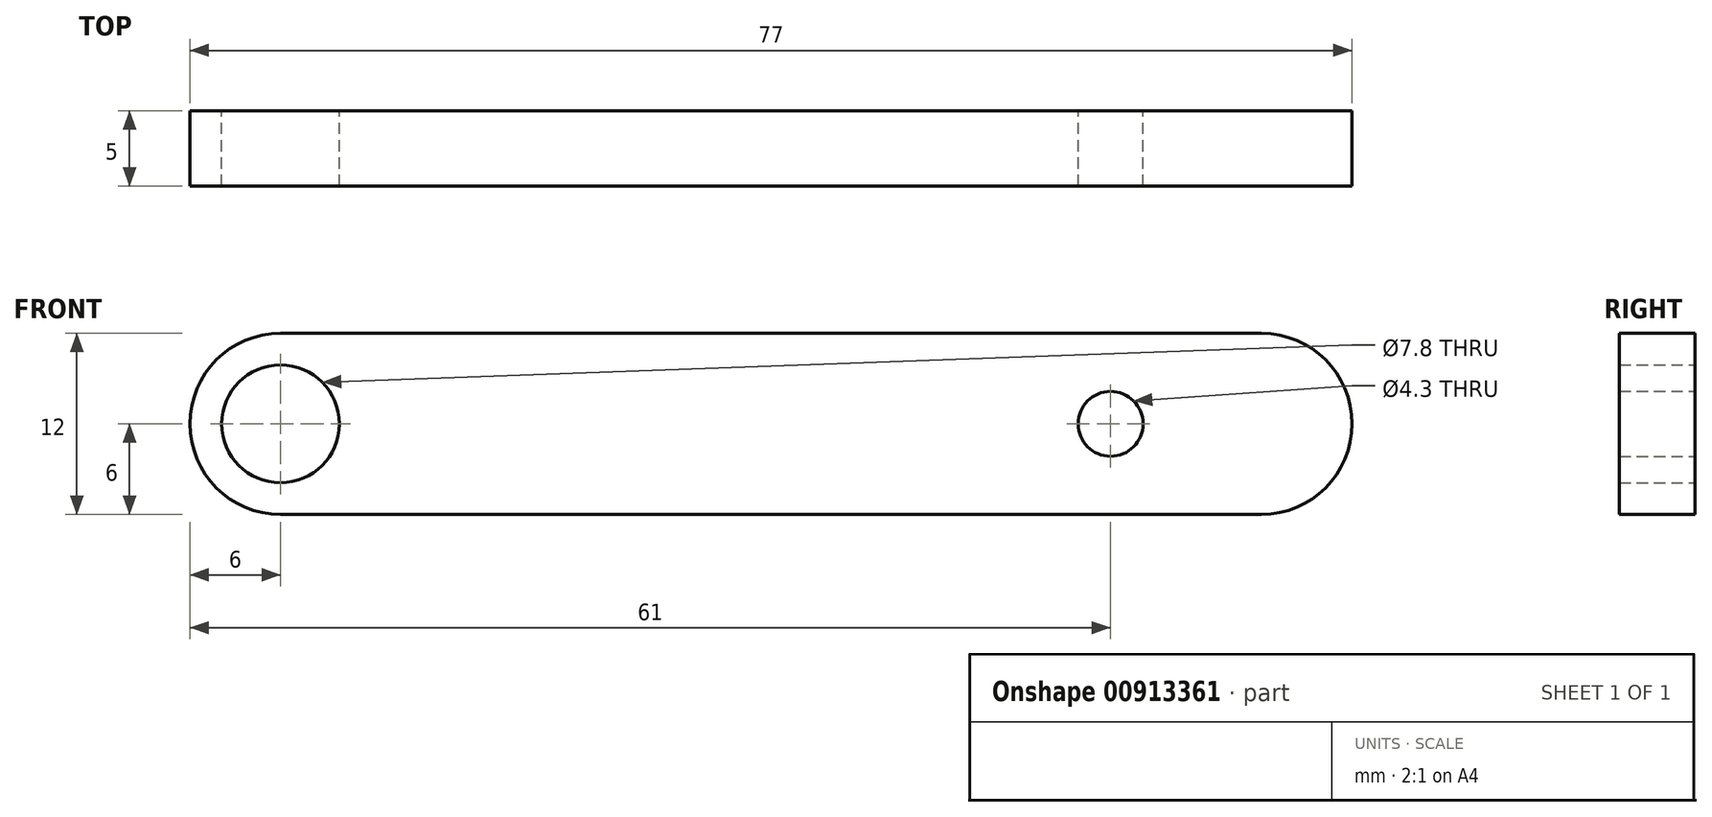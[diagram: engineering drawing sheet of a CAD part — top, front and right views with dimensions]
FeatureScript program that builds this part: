
annotation { "Feature Type Name" : "Feature", "Feature Type Description" : "" }
export const myFeature = defineFeature(function(context is Context, id is Id, definition is map)
    precondition{}
    {
        {
            var Q0;
            Q0=qCreatedBy(makeId("Front.planeOp"),FACE);
            var sketch = newSketch(context, id + "F0", { "sketchPlane" : qUnion([Q0])});
            skArc(sketch, "E0", {"start": v(0, 6) * mm, "mid": v(-6, 0) * mm, "end": v(0, -6) * mm});
            skCircle(sketch, "E1", {"center": v(0, 0) * mm, "radius": 3.9 * mm});
            skArc(sketch, "E2", {"start": v(65, -6) * mm, "mid": v(71, 0) * mm, "end": v(65, 6) * mm});
            skLineSegment(sketch, "E3", {"start": v(0, 6) * mm, "end": v(65, 6) * mm});
            skLineSegment(sketch, "E4", {"start": v(0, -6) * mm, "end": v(65, -6) * mm});
            skCircle(sketch, "E5", {"center": v(55, 0) * mm, "radius": 2.15 * mm});
            skSolve(sketch);
        }
        {
            var Q0;
            Q0 = qSketchRegion(id + "F0", true);
            extrude(context, id + "F1", {"entities" : qUnion([Q0]), "depth" : 5 * mm, "offsetDistance" : 25 * mm, "symmetric" : true});
        }
    });
